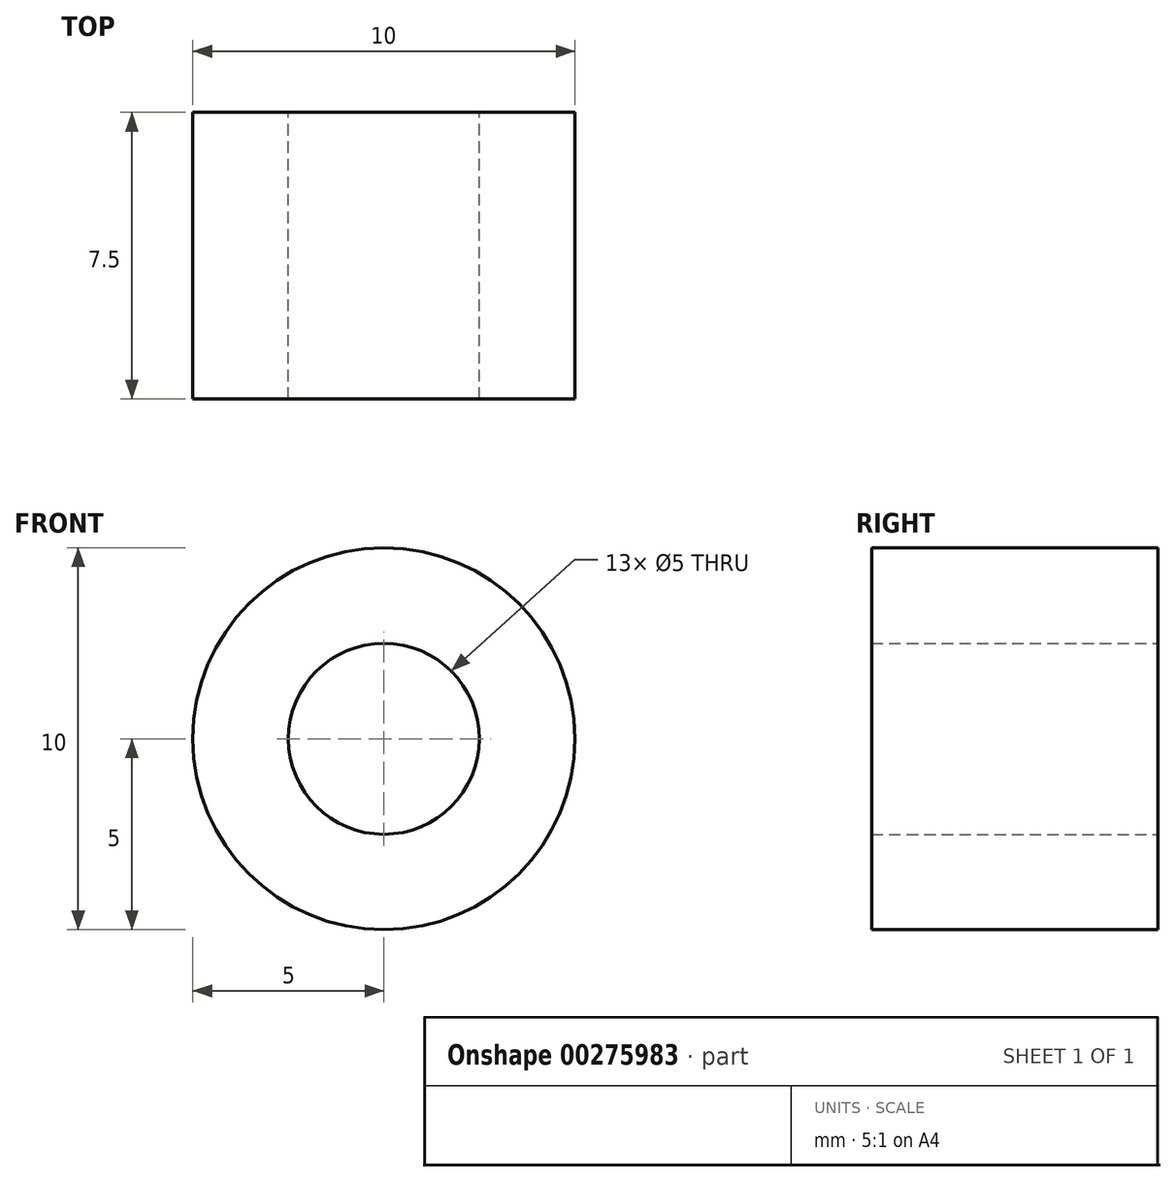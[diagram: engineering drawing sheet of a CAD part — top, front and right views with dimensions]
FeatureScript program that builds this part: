
annotation { "Feature Type Name" : "Feature", "Feature Type Description" : "" }
export const myFeature = defineFeature(function(context is Context, id is Id, definition is map)
    precondition{}
    {
        {
            var Q0;
            Q0=qCreatedBy(makeId("Front.planeOp"),FACE);
            var sketch = newSketch(context, id + "F0", { "sketchPlane" : qUnion([Q0])});
            skCircle(sketch, "E0", {"center": v(0, 0) * mm, "radius": 2.5 * mm});
            skCircle(sketch, "E1", {"center": v(0, 0) * mm, "radius": 5 * mm});
            skSolve(sketch);
        }
        {
            var Q0;
            Q0=makeQuery(id+"F0.imprint","IMPRINT",FACE,{"disambiguationData":[TD([[makeQuery(id+"F0.imprint","IMPRINT",EDGE,{"derivedFrom":sQuery(id+"F0.wireOp",EDGE,"E0")}),-1.0]])]});
            extrude(context, id + "F1", {"entities" : qUnion([Q0]), "depth" : 7.5 * mm});
        }
    });
